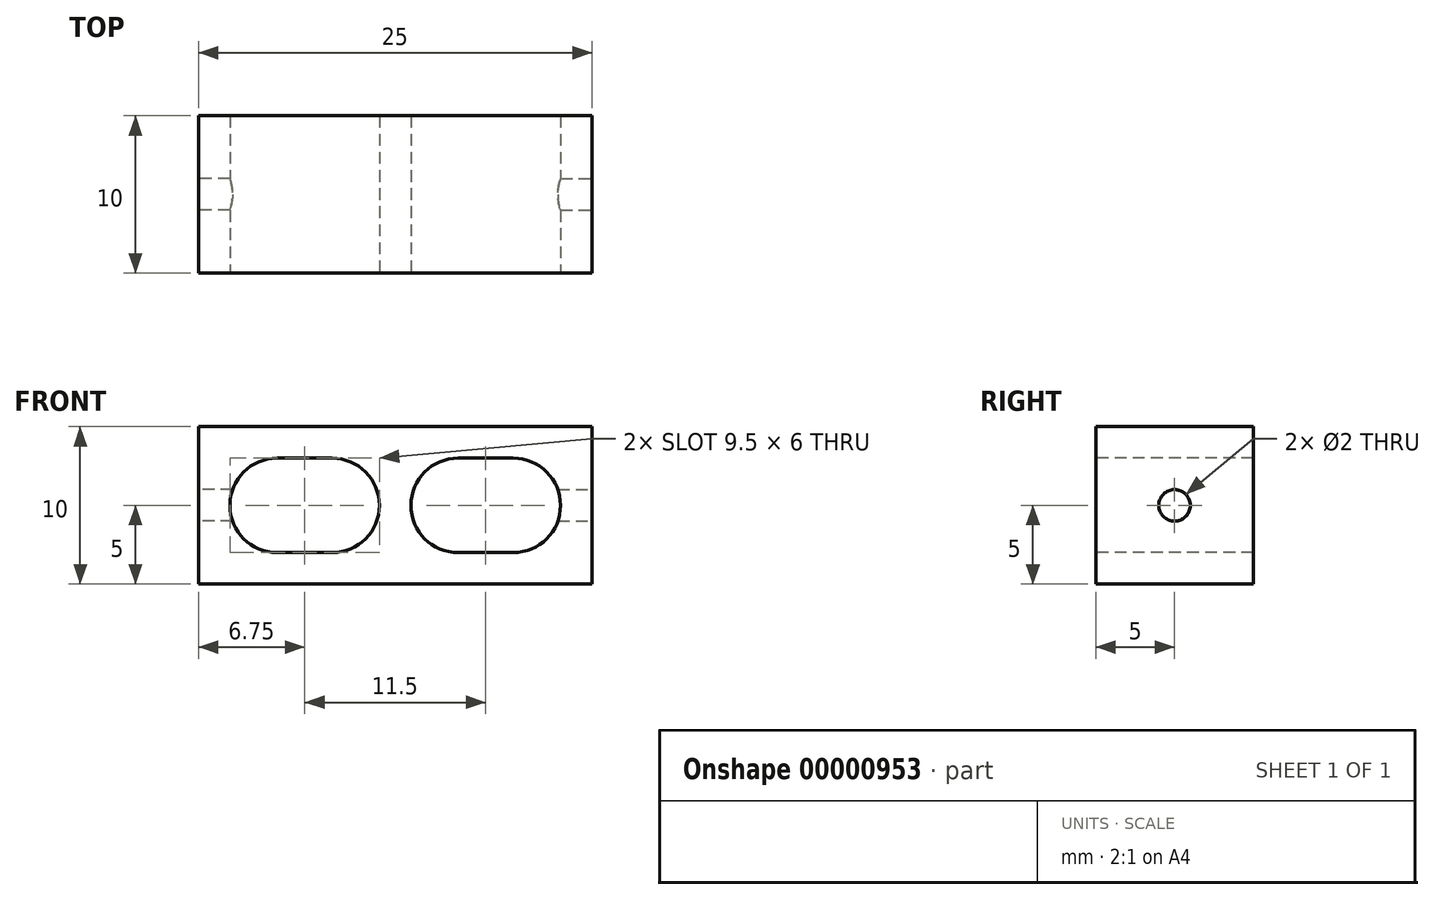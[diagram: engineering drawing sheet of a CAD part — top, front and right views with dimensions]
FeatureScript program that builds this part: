
annotation { "Feature Type Name" : "Feature", "Feature Type Description" : "" }
export const myFeature = defineFeature(function(context is Context, id is Id, definition is map)
    precondition{}
    {
        {
            var Q0;
            Q0=qCreatedBy(makeId("Top.planeOp"),FACE);
            var sketch = newSketch(context, id + "F0", { "sketchPlane" : qUnion([Q0])});
            skLineSegment(sketch, "E0.bottom", {"start": v(12.5, -5) * mm, "end": v(-12.5, -5) * mm});
            skLineSegment(sketch, "E0.top", {"start": v(12.5, 5) * mm, "end": v(-12.5, 5) * mm});
            skLineSegment(sketch, "E0.left", {"start": v(12.5, -5) * mm, "end": v(12.5, 5) * mm});
            skLineSegment(sketch, "E0.right", {"start": v(-12.5, -5) * mm, "end": v(-12.5, 5) * mm});
            skPoint(sketch, "E0.middle", {"position": v(0, 0) * mm});
            skSolve(sketch);
        }
        {
            var Q0;
            Q0=makeQuery(id+"F0.imprint","IMPRINT",FACE,{"disambiguationData":[TD([[makeQuery(id+"F0.imprint","IMPRINT",EDGE,{"derivedFrom":sQuery(id+"F0.wireOp",EDGE,"E0.bottom")}),-1.0]])]});
            extrude(context, id + "F1", {"entities" : qUnion([Q0]), "endBound" : BoundingType.SYMMETRIC, "depth" : 10 * mm});
        }
        {
            var Q0;
            Q0=qCreatedBy(makeId("Front.planeOp"),FACE);
            var sketch = newSketch(context, id + "F2", { "sketchPlane" : qUnion([Q0])});
            skLineSegment(sketch, "E1", {"start": v(-7.5, 3) * mm, "end": v(-4, 3) * mm});
            skLineSegment(sketch, "E2", {"start": v(-7.5, -3) * mm, "end": v(-4, -3) * mm});
            skArc(sketch, "E3", {"start": v(-4, 3) * mm, "mid": v(-1, 0) * mm, "end": v(-4, -3) * mm});
            skArc(sketch, "E4", {"start": v(-7.5, 3) * mm, "mid": v(-10.5, 0) * mm, "end": v(-7.5, -3) * mm});
            skSolve(sketch);
        }
        {
            var Q0;
            Q0 = qSketchRegion(id + "F2", true);
            extrude(context, id + "F3", {"entities" : qUnion([Q0]), "operationType" : NewBodyOperationType.REMOVE, "endBound" : BoundingType.THROUGH_ALL, "oppositeDirection" : true, "depth" : 25 * mm, "hasSecondDirection" : true, "secondDirectionBound" : SecondDirectionBoundingType.THROUGH_ALL, "secondDirectionOppositeDirection" : false, "secondDirectionDepth" : 25 * mm});
        }
        {
            var Q0;
            Q0=makeQuery(id+"F1.opExtrude","SWEPT_FACE",FACE,{"disambiguationData":[OSD([sQuery(id+"F0.wireOp",EDGE,"E0.right")])]});
            var sketch = newSketch(context, id + "F4", { "sketchPlane" : qUnion([Q0])});
            skCircle(sketch, "E5", {"center": v(0, 0) * mm, "radius": 1 * mm});
            skSolve(sketch);
        }
        {
            var Q0;
            Q0=makeQuery(id+"F4.imprint","IMPRINT",FACE,{"disambiguationData":[TD([[makeQuery(id+"F4.imprint","IMPRINT",EDGE,{"derivedFrom":sQuery(id+"F4.wireOp",EDGE,"E5")}),1.0]])]});
            extrude(context, id + "F5", {"entities" : qUnion([Q0]), "operationType" : NewBodyOperationType.REMOVE, "endBound" : BoundingType.UP_TO_NEXT, "oppositeDirection" : true, "depth" : 25 * mm});
        }
        {
            var Q0;
            Q0=makeQuery(id+"F3.boolean.opBoolean","COPY",FACE,{"derivedFrom":makeQuery(id+"F3.opExtrude","SWEPT_FACE",FACE,{"disambiguationData":[OSD([sQuery(id+"F2.wireOp",EDGE,"E4")])]})});
            var Q1;
            Q1=makeQuery(id+"F3.boolean.opBoolean","COPY",FACE,{"derivedFrom":makeQuery(id+"F3.opExtrude","SWEPT_FACE",FACE,{"disambiguationData":[OSD([sQuery(id+"F2.wireOp",EDGE,"E2")])]})});
            var Q2;
            Q2=makeQuery(id+"F3.boolean.opBoolean","COPY",FACE,{"derivedFrom":makeQuery(id+"F3.opExtrude","SWEPT_FACE",FACE,{"disambiguationData":[OSD([sQuery(id+"F2.wireOp",EDGE,"E1")])]})});
            var Q3;
            Q3=makeQuery(id+"F5.boolean.opBoolean","COPY",FACE,{"derivedFrom":makeQuery(id+"F5.opExtrude","SWEPT_FACE",FACE,{"disambiguationData":[OSD([sQuery(id+"F4.wireOp",EDGE,"E5")])]})});
            var Q4;
            Q4=makeQuery(id+"F3.boolean.opBoolean","COPY",FACE,{"derivedFrom":makeQuery(id+"F3.opExtrude","SWEPT_FACE",FACE,{"disambiguationData":[OSD([sQuery(id+"F2.wireOp",EDGE,"E3")])]})});
            var Q5;
            Q5=qCreatedBy(makeId("Right.planeOp"),FACE);
            mirror(context, id + "F6", {"faces" : qUnion([Q0, Q1, Q2, Q3, Q4]), "mirrorPlane" : qUnion([Q5]), "patternType" : MirrorType.FACE});
        }
    });
